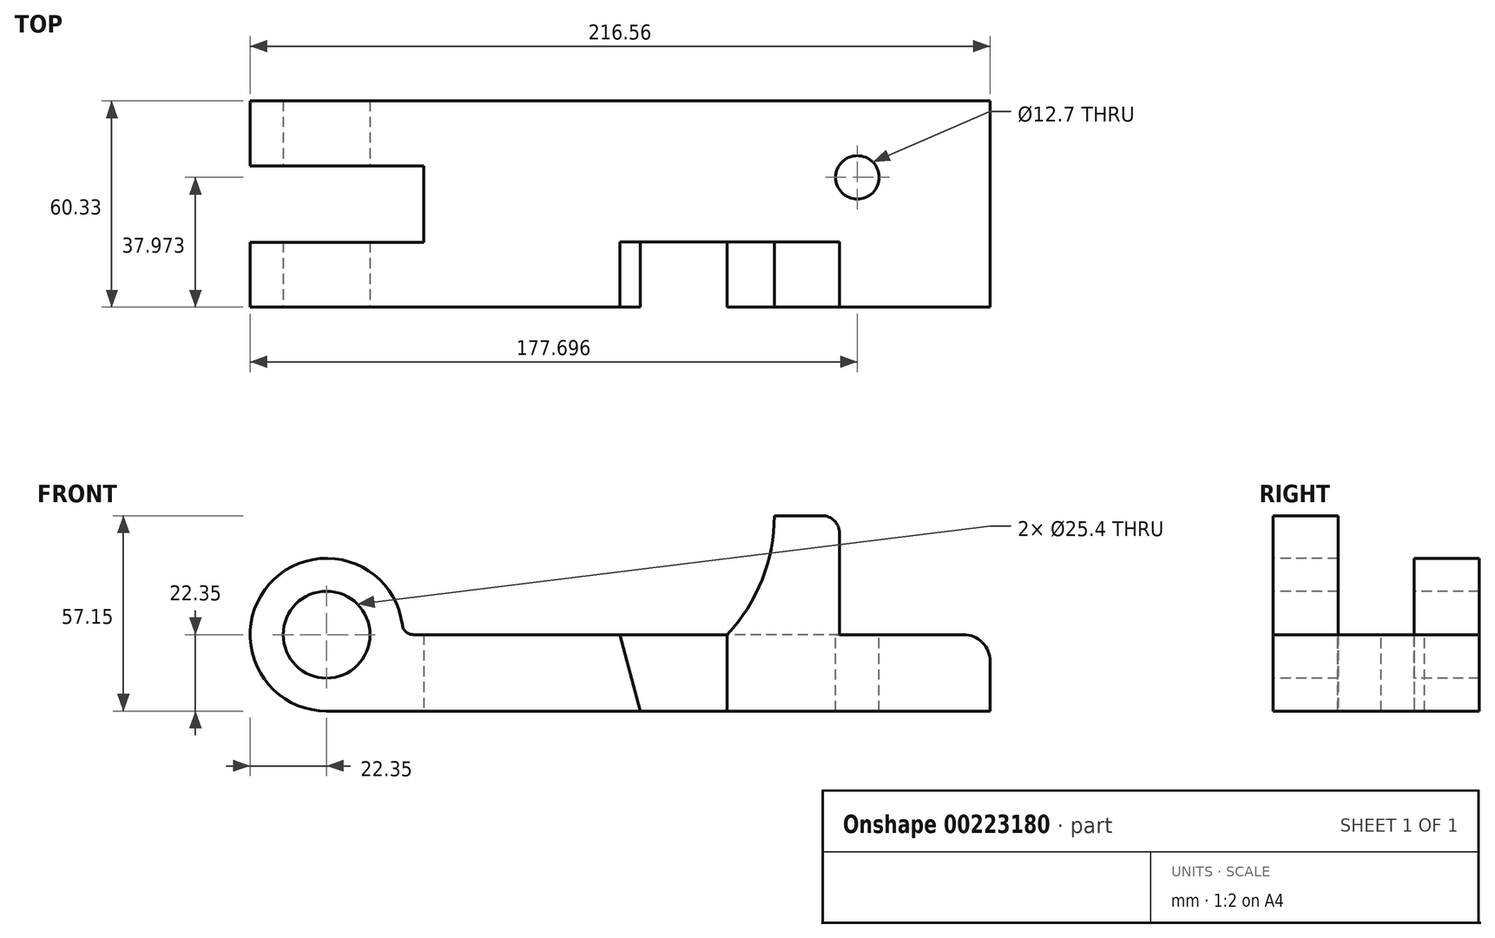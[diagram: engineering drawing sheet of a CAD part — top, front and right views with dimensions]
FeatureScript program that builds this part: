
annotation { "Feature Type Name" : "Feature", "Feature Type Description" : "" }
export const myFeature = defineFeature(function(context is Context, id is Id, definition is map)
    precondition{}
    {
        {
            var Q0;
            Q0=qCreatedBy(makeId("Front.planeOp"),FACE);
            var sketch = newSketch(context, id + "F0", { "sketchPlane" : qUnion([Q0])});
            skCircle(sketch, "E0", {"center": v(0, 0) * mm, "radius": 22.35 * mm});
            skLineSegment(sketch, "E1", {"start": v(0, -22.35) * mm, "end": v(194.2, -22.35) * mm});
            skLineSegment(sketch, "E2", {"start": v(194.2, -22.35) * mm, "end": v(194.2, 0) * mm});
            skLineSegment(sketch, "E3", {"start": v(194.2, 0) * mm, "end": v(22.35, 0) * mm});
            skCircle(sketch, "E4", {"center": v(0, 0) * mm, "radius": 12.7 * mm});
            skSolve(sketch);
        }
        {
            var Q0;
            {var subQ0=sQuery(id+"F0.wireOp",EDGE,"E1");Q0=makeQuery(id+"F0.imprint","IMPRINT",FACE,{"disambiguationData":[TD([[makeQuery(id+"F0.imprint","IMPRINT",EDGE,{"derivedFrom":subQ0}),1.0]])]});}
            var Q1;
            {var subQ0=sQuery(id+"F0.wireOp",EDGE,"E0");var subQ1=makeQuery(id+"F0.imprint","INTERSECT",VERTEX,{"derivedFrom":[subQ0,sQuery(id+"F0.wireOp",EDGE,"E1")]});Q1=makeQuery(id+"F0.imprint","IMPRINT",FACE,{"disambiguationData":[TD([[makeQuery(id+"F0.imprint","IMPRINT",EDGE,{"disambiguationData":[TD([[subQ1,1.0]])],"derivedFrom":subQ0}),1.0]])]});}
            extrude(context, id + "F1", {"entities" : qUnion([Q0, Q1]), "oppositeDirection" : true, "depth" : 60.32 * mm});
        }
        {
            var Q0;
            Q0=makeQuery(id+"F1.opExtrude","SWEPT_EDGE",EDGE,{"disambiguationData":[OSD([sQuery(id+"F0.wireOp",EDGE,"E2"),sQuery(id+"F0.wireOp",EDGE,"E3")])]});
            fillet(context, id + "F2", {"entities" : qUnion([Q0]), "radius" : 7.87 * mm, "tangentPropagation" : true, "allowEdgeOverflow" : false});
        }
        {
            var Q0;
            {var subQ0=sQuery(id+"F0.wireOp",EDGE,"E1");Q0=makeQuery(id+"F0.imprint","IMPRINT",FACE,{"disambiguationData":[TD([[makeQuery(id+"F0.imprint","IMPRINT",EDGE,{"derivedFrom":subQ0}),1.0]])]});}
            var sketch = newSketch(context, id + "F3", { "sketchPlane" : qUnion([Q0])});
            skLineSegment(sketch, "E5", {"start": v(117.25, 0) * mm, "end": v(150.09, 0) * mm});
            skLineSegment(sketch, "E6", {"start": v(150.09, 0) * mm, "end": v(150.09, 34.8) * mm});
            skLineSegment(sketch, "E7", {"start": v(150.09, 34.8) * mm, "end": v(131.04, 34.8) * mm});
            skArc(sketch, "E8", {"start": v(117.25, 0) * mm, "mid": v(127.46, 16.08) * mm, "end": v(131.04, 34.8) * mm});
            skLineSegment(sketch, "E9", {"start": v(117.25, 0) * mm, "end": v(117.25, -15.1) * mm, "construction": true});
            skSolve(sketch);
        }
        {
            var Q0;
            Q0 = qSketchRegion(id + "F3", true);
            extrude(context, id + "F4", {"entities" : qUnion([Q0]), "operationType" : NewBodyOperationType.ADD, "oppositeDirection" : true, "depth" : 19.05 * mm});
        }
        {
            var Q0;
            Q0=makeQuery(id+"F4.boolean.opBoolean","MERGE",FACE,{"derivedFrom":[makeQuery(id+"F1.opExtrude","CAP_FACE",FACE,{"disambiguationData":[OSD([sQuery(id+"F0.wireOp",EDGE,"E0"),sQuery(id+"F0.wireOp",EDGE,"E1"),sQuery(id+"F0.wireOp",EDGE,"E2"),sQuery(id+"F0.wireOp",EDGE,"E3"),sQuery(id+"F0.wireOp",EDGE,"E4")])],"isStart":true}),makeQuery(id+"F4.opExtrude","CAP_FACE",FACE,{"disambiguationData":[OSD([sQuery(id+"F3.wireOp",EDGE,"E5"),sQuery(id+"F3.wireOp",EDGE,"E6"),sQuery(id+"F3.wireOp",EDGE,"E7"),sQuery(id+"F3.wireOp",EDGE,"E8")])],"isStart":true})]});
            var sketch = newSketch(context, id + "F5", { "sketchPlane" : qUnion([Q0])});
            skLineSegment(sketch, "E10", {"start": v(117.25, 0) * mm, "end": v(85.85, 0) * mm});
            skLineSegment(sketch, "E11", {"start": v(85.85, 0) * mm, "end": v(91.85, -22.35) * mm});
            skLineSegment(sketch, "E12", {"start": v(91.85, -22.35) * mm, "end": v(117.25, -22.35) * mm});
            skLineSegment(sketch, "E13", {"start": v(117.25, -22.35) * mm, "end": v(117.25, 0) * mm});
            skSolve(sketch);
        }
        {
            var Q0;
            Q0 = qSketchRegion(id + "F5", true);
            extrude(context, id + "F6", {"entities" : qUnion([Q0]), "operationType" : NewBodyOperationType.REMOVE, "oppositeDirection" : true, "depth" : 19.05 * mm});
        }
        {
            var Q0;
            Q0=makeQuery(id+"F4.opExtrude","SWEPT_EDGE",EDGE,{"disambiguationData":[OSD([sQuery(id+"F3.wireOp",EDGE,"E6"),sQuery(id+"F3.wireOp",EDGE,"E7")])]});
            fillet(context, id + "F7", {"entities" : qUnion([Q0]), "radius" : 5.08 * mm, "tangentPropagation" : true, "allowEdgeOverflow" : false});
        }
        {
            var Q0;
            Q0=makeQuery(id+"F1.opExtrude","SWEPT_FACE",FACE,{"disambiguationData":[OSD([sQuery(id+"F0.wireOp",EDGE,"E3")])]});
            var sketch = newSketch(context, id + "F8", { "sketchPlane" : qUnion([Q0])});
            skCircle(sketch, "E14", {"center": v(155.35, 37.97) * mm, "radius": 6.35 * mm});
            skSolve(sketch);
        }
        {
            var Q0;
            Q0 = qSketchRegion(id + "F8", true);
            extrude(context, id + "F9", {"entities" : qUnion([Q0]), "operationType" : NewBodyOperationType.REMOVE, "endBound" : BoundingType.THROUGH_ALL, "oppositeDirection" : true, "depth" : 25.4 * mm});
        }
        {
            var Q0;
            Q0=makeQuery(id+"F1.opExtrude","SWEPT_FACE",FACE,{"disambiguationData":[OSD([sQuery(id+"F0.wireOp",EDGE,"E1")])]});
            var sketch = newSketch(context, id + "F10", { "sketchPlane" : qUnion([Q0])});
            skLineSegment(sketch, "E15", {"start": v(-22.35, -41.33) * mm, "end": v(-22.35, -19) * mm});
            skLineSegment(sketch, "E16", {"start": v(-22.35, -19) * mm, "end": v(28.45, -19) * mm});
            skLineSegment(sketch, "E17", {"start": v(28.45, -19) * mm, "end": v(28.45, -41.33) * mm});
            skLineSegment(sketch, "E18", {"start": v(28.45, -41.33) * mm, "end": v(-22.35, -41.33) * mm});
            skSolve(sketch);
        }
        {
            var Q0;
            Q0 = qSketchRegion(id + "F10", true);
            extrude(context, id + "F11", {"entities" : qUnion([Q0]), "operationType" : NewBodyOperationType.REMOVE, "oppositeDirection" : true, "depth" : 44.7 * mm});
        }
        {
            var Q0;
            {var subQ0=sQuery(id+"F0.wireOp",EDGE,"E3");var subQ1=sQuery(id+"F0.wireOp",EDGE,"E0");Q0=makeQuery(id+"F11.boolean.opBoolean","SPLIT",EDGE,{"disambiguationData":[TD([makeQuery(id+"F1.opExtrude","SWEPT_FACE",FACE,{"disambiguationData":[OSD([subQ1])]}),makeQuery(id+"F1.opExtrude","CAP_FACE",FACE,{"disambiguationData":[OSD([subQ1,sQuery(id+"F0.wireOp",EDGE,"E1"),sQuery(id+"F0.wireOp",EDGE,"E2"),subQ0,sQuery(id+"F0.wireOp",EDGE,"E4")])],"isStart":true}),makeQuery(id+"F1.opExtrude","SWEPT_FACE",FACE,{"disambiguationData":[OSD([subQ0])]}),makeQuery(id+"F4.opExtrude","CAP_FACE",FACE,{"disambiguationData":[OSD([sQuery(id+"F3.wireOp",EDGE,"E5"),sQuery(id+"F3.wireOp",EDGE,"E6"),sQuery(id+"F3.wireOp",EDGE,"E7"),sQuery(id+"F3.wireOp",EDGE,"E8")])],"isStart":true}),makeQuery(id+"F11.opExtrude","SWEPT_FACE",FACE,{"disambiguationData":[OSD([sQuery(id+"F10.wireOp",EDGE,"E16")])]}),makeQuery(id+"F11.opExtrude","SWEPT_FACE",FACE,{"disambiguationData":[OSD([sQuery(id+"F10.wireOp",EDGE,"E17")])]})])],"derivedFrom":makeQuery(id+"F1.opExtrude","SWEPT_EDGE",EDGE,{"disambiguationData":[OSD([subQ1,subQ0])]})});}
            var Q1;
            {var subQ0=sQuery(id+"F0.wireOp",EDGE,"E3");var subQ1=sQuery(id+"F0.wireOp",EDGE,"E0");Q1=makeQuery(id+"F11.boolean.opBoolean","SPLIT",EDGE,{"disambiguationData":[TD([makeQuery(id+"F1.opExtrude","SWEPT_FACE",FACE,{"disambiguationData":[OSD([subQ1])]}),makeQuery(id+"F1.opExtrude","CAP_FACE",FACE,{"disambiguationData":[OSD([subQ1,sQuery(id+"F0.wireOp",EDGE,"E1"),sQuery(id+"F0.wireOp",EDGE,"E2"),subQ0,sQuery(id+"F0.wireOp",EDGE,"E4")])],"isStart":false}),makeQuery(id+"F1.opExtrude","SWEPT_FACE",FACE,{"disambiguationData":[OSD([subQ0])]}),makeQuery(id+"F11.opExtrude","SWEPT_FACE",FACE,{"disambiguationData":[OSD([sQuery(id+"F10.wireOp",EDGE,"E17")])]}),makeQuery(id+"F11.opExtrude","SWEPT_FACE",FACE,{"disambiguationData":[OSD([sQuery(id+"F10.wireOp",EDGE,"E18")])]})])],"derivedFrom":makeQuery(id+"F1.opExtrude","SWEPT_EDGE",EDGE,{"disambiguationData":[OSD([subQ1,subQ0])]})});}
            var Q2;
            Q2=makeQuery(id+"F4.opExtrude","SWEPT_EDGE",EDGE,{"disambiguationData":[OSD([sQuery(id+"F0.wireOp",EDGE,"E3"),sQuery(id+"F3.wireOp",EDGE,"E5"),sQuery(id+"F3.wireOp",EDGE,"E6")])]});
            fillet(context, id + "F12", {"entities" : qUnion([Q0, Q1, Q2]), "radius" : 3.3 * mm, "tangentPropagation" : true, "allowEdgeOverflow" : false});
        }
    });
